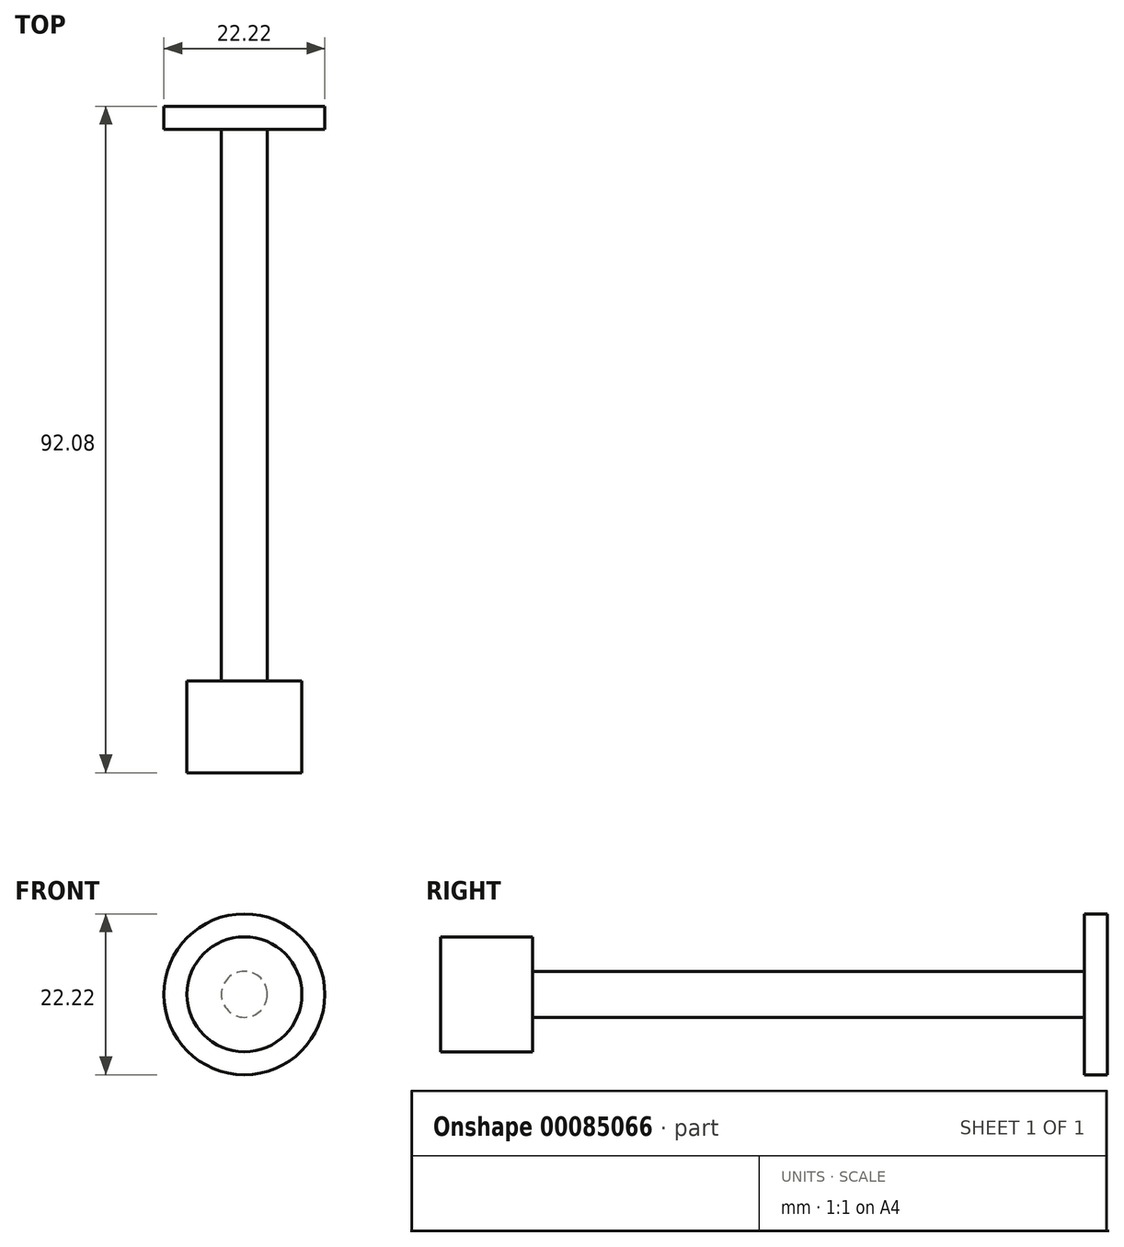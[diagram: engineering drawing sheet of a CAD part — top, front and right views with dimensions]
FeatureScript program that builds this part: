
annotation { "Feature Type Name" : "Feature", "Feature Type Description" : "" }
export const myFeature = defineFeature(function(context is Context, id is Id, definition is map)
    precondition{}
    {
        {
            var Q0;
            Q0=qCreatedBy(makeId("Front.planeOp"),FACE);
            var sketch = newSketch(context, id + "F0", { "sketchPlane" : qUnion([Q0])});
            skCircle(sketch, "E0", {"center": v(0, 0) * mm, "radius": 11.11 * mm});
            skSolve(sketch);
        }
        {
            var Q0;
            Q0 = qSketchRegion(id + "F0", true);
            extrude(context, id + "F1", {"entities" : qUnion([Q0]), "depth" : 3.17 * mm});
        }
        {
            var Q0;
            Q0=makeQuery(id+"F1.opExtrude","CAP_FACE",FACE,{"disambiguationData":[OSD([sQuery(id+"F0.wireOp",EDGE,"E0")])],"isStart":false});
            var sketch = newSketch(context, id + "F2", { "sketchPlane" : qUnion([Q0])});
            skPoint(sketch, "E1.0", {"position": v(0, 0) * mm});
            skCircle(sketch, "E2", {"center": v(0, 0) * mm, "radius": 3.18 * mm});
            skSolve(sketch);
        }
        {
            var Q0;
            Q0 = qSketchRegion(id + "F2", true);
            extrude(context, id + "F3", {"entities" : qUnion([Q0]), "operationType" : NewBodyOperationType.ADD, "depth" : 76.2 * mm});
        }
        {
            var Q0;
            Q0=makeQuery(id+"F3.opExtrude","CAP_FACE",FACE,{"disambiguationData":[OSD([sQuery(id+"F2.wireOp",EDGE,"E2")])],"isStart":false});
            var sketch = newSketch(context, id + "F4", { "sketchPlane" : qUnion([Q0])});
            skPoint(sketch, "E3.0", {"position": v(0, 0) * mm});
            skCircle(sketch, "E4", {"center": v(0, 0) * mm, "radius": 7.94 * mm});
            skSolve(sketch);
        }
        {
            var Q0;
            Q0 = qSketchRegion(id + "F4", true);
            extrude(context, id + "F5", {"entities" : qUnion([Q0]), "operationType" : NewBodyOperationType.ADD, "depth" : 12.7 * mm});
        }
    });
